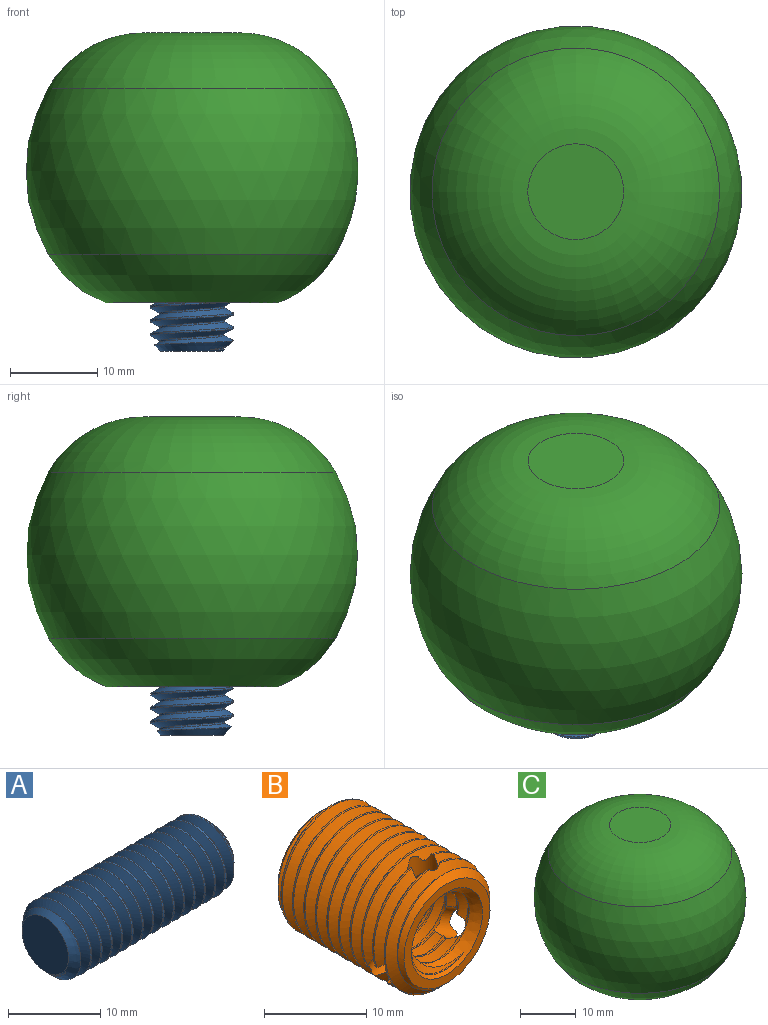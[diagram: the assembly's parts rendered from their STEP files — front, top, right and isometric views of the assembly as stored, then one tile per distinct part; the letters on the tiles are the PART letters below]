
ASSEMBLY  parts=3 mates=2
PART A: 9 faces, bbox 26.7x9.7x9.7 mm
  f0: cone r=4.76mm half-angle=45deg, axis (1,0,0), area 22.8mm2, adj f1,f4,f6,f7,f8
  f1: cone r=4.76mm half-angle=45deg, axis (1,0,0), area 1.2mm2, adj f0,f3,f6
  f2: cone r=3.57mm half-angle=45deg, axis (-1,0,0), area 24mm2, adj f3,f5,f6,f7,f8
  f3: cylinder r=4.76mm len=23.02mm, axis (1,0,0), area 85.9mm2, adj f1,f2,f6,f8
  f4: plane 7.14x7.14mm, normal (-1,0,0), area 40.1mm2, adj f0
  f5: plane 7.14x7.14mm, normal (1,0,0), area 40.1mm2, adj f2
  f6: bspline ~26.05x9.7mm, area 481.6mm2, adj f0,f1,f2,f3,f7
  f7: cylinder r=3.73mm len=25.08mm, axis (1,0,0), area 72.8mm2, adj f0,f2,f6,f8
  f8: bspline ~26.05x9.7mm, area 479.2mm2, adj f0,f2,f3,f7
PART B: 59 faces, bbox 14.5x18.5x14.5 mm
  f0: cylinder r=7.15mm len=9.12mm, axis (0,1,0), area 2.3mm2, adj f33,f44,f56,f57
  f1: cylinder r=7.15mm len=10.68mm, axis (0,1,0), area 2.4mm2, adj f34,f45,f57,f58
  f2: cylinder r=7.15mm len=9.5mm, axis (0,1,0), area 2.5mm2, adj f35,f46,f56,f58
  f3: cylinder r=7.15mm len=11.26mm, axis (0,1,0), area 2.5mm2, adj f31,f42,f57,f58
  f4: cylinder r=7.15mm len=14.3mm, axis (0,1,0), area 66mm2, adj f30,f42,f50,f57
  f5: cylinder r=7.15mm len=9.35mm, axis (0,1,0), area 2.4mm2, adj f32,f43,f56,f58
  f6: cylinder r=3.73mm len=3.72mm, axis (0,1,0), area 0.9mm2, adj f14,f27,f56,f57
  f7: cylinder r=3.73mm len=4.5mm, axis (0,1,0), area 0.9mm2, adj f15,f28,f57,f58
  f8: cylinder r=3.73mm len=4.3mm, axis (0,1,0), area 1.1mm2, adj f16,f29,f56,f58
  f9: cylinder r=3.73mm len=5.21mm, axis (0,1,0), area 1.1mm2, adj f12,f25,f57,f58
  f10: cylinder r=3.73mm len=11.78mm, axis (0,1,0), area 33.9mm2, adj f12,f24,f52,f57
  f11: cylinder r=3.73mm len=3.97mm, axis (0,1,0), area 0.9mm2, adj f13,f26,f56,f58
  f12: bspline ~13.25x9.18mm, area 210mm2, adj f9,f10,f18,f52,f57,f58
  f13: bspline ~6.86x4.21mm, area 6.1mm2, adj f11,f18,f56,f58
  f14: bspline ~6.08x4.06mm, area 5.5mm2, adj f6,f19,f56,f57
  f15: bspline ~6.49x2.01mm, area 5.5mm2, adj f7,f20,f57,f58
  f16: bspline ~6.03x4.05mm, area 5.9mm2, adj f8,f21,f56,f58
  f17: bspline ~9.18x9.18mm, area 22.1mm2, adj f22,f23,f49,f53,f56,f57
  f18: cylinder r=4.59mm len=12.99mm, axis (0,-1,0), area 80mm2, adj f12,f13,f24,f52,f56,f58
  f19: cylinder r=4.59mm len=5.5mm, axis (0,-1,0), area 2.8mm2, adj f14,f24,f56,f57
  f20: cylinder r=4.59mm len=6.02mm, axis (0,-1,0), area 2.6mm2, adj f15,f25,f57,f58
  f21: cylinder r=4.59mm len=5.16mm, axis (0,-1,0), area 2.6mm2, adj f16,f26,f56,f58
  f22: cylinder r=4.59mm len=5.69mm, axis (0,-1,0), area 2.7mm2, adj f17,f27,f56,f57
  f23: cylinder r=4.59mm len=9.18mm, axis (0,-1,0), area 12.6mm2, adj f17,f28,f29,f53,f57,f58
  f24: bspline ~13.65x9.18mm, area 207.3mm2, adj f10,f18,f19,f52,f56,f57
  f25: bspline ~6.11x1.88mm, area 5.9mm2, adj f9,f20,f57,f58
  f26: bspline ~5.1x3.31mm, area 5.5mm2, adj f11,f21,f56,f58
  f27: bspline ~6.18x3.92mm, area 5.5mm2, adj f6,f22,f56,f57
  f28: bspline ~7.17x2.7mm, area 6mm2, adj f7,f23,f57,f58
  f29: bspline ~9.18x9.18mm, area 20.2mm2, adj f8,f23,f49,f53,f56,f58
  f30: bspline ~14.47x14.47mm, area 392.9mm2, adj f4,f36,f37,f50,f56,f57
  f31: bspline ~12.66x4.41mm, area 13.2mm2, adj f3,f38,f57,f58
  f32: bspline ~10.71x6.97mm, area 12.8mm2, adj f5,f39,f56,f58
  f33: bspline ~10.61x6.95mm, area 13mm2, adj f0,f40,f56,f57
  f34: bspline ~11.1x3.53mm, area 13.7mm2, adj f1,f41,f57,f58
  f35: bspline ~14.47x14.47mm, area 40.3mm2, adj f2,f41,f48,f51,f56,f58
  f36: cylinder r=6.12mm len=13.09mm, axis (0,-1,0), area 44.7mm2, adj f30,f42,f43,f50,f56,f58
  f37: cylinder r=6.12mm len=7.76mm, axis (0,-1,0), area 2mm2, adj f30,f44,f56,f57
  f38: cylinder r=6.12mm len=8.74mm, axis (0,-1,0), area 1.9mm2, adj f31,f45,f57,f58
  f39: cylinder r=6.12mm len=7.52mm, axis (0,-1,0), area 1.9mm2, adj f32,f46,f56,f58
  f40: cylinder r=6.12mm len=7.95mm, axis (0,-1,0), area 2mm2, adj f33,f47,f56,f57
  f41: cylinder r=6.12mm len=12.24mm, axis (0,-1,0), area 9.3mm2, adj f34,f35,f47,f51,f57,f58
  f42: bspline ~14.47x14.47mm, area 386.8mm2, adj f3,f4,f36,f50,f57,f58
  f43: bspline ~10x5.94mm, area 13.8mm2, adj f5,f36,f56,f58
  f44: bspline ~9.1x5.86mm, area 13mm2, adj f0,f37,f56,f57
  f45: bspline ~12.27x4.03mm, area 12.8mm2, adj f1,f38,f57,f58
  f46: bspline ~9.35x6.23mm, area 13.2mm2, adj f2,f39,f56,f58
  f47: bspline ~14.29x14.28mm, area 46.4mm2, adj f40,f41,f48,f51,f56,f57
  f48: cylinder r=7.15mm len=14.26mm, axis (0,1,0), area 3.7mm2, adj f35,f47,f51,f56
  f49: cylinder r=3.73mm len=7.4mm, axis (0,1,0), area 1.8mm2, adj f17,f29,f53,f56
  f50: cone r=5.96mm half-angle=45deg, axis (0,-1,0), area 38.4mm2, adj f4,f30,f36,f42,f55
  f51: cone r=7.15mm half-angle=45deg, axis (0,1,0), area 38.4mm2, adj f35,f41,f47,f48,f54
  f52: cone r=3.73mm half-angle=45deg, axis (0,1,0), area 28.3mm2, adj f10,f12,f18,f24,f55
  f53: cone r=4.92mm half-angle=45deg, axis (0,-1,0), area 28.3mm2, adj f17,f23,f29,f49,f54
  f54: plane 11.92x11.92mm, normal (0,-1,0), area 35.5mm2, adj f51,f53
  f55: plane 11.92x11.92mm, normal (0,1,0), area 35.5mm2, adj f50,f52
  f56: cylinder r=1.59mm len=3.74mm, axis (0,0,-1), area 25.5mm2, adj f0,f2,f5,f6,f8,f11,f13,f14
  f57: cylinder r=1.59mm len=4.83mm, axis (0.87,0,0.5), area 25.8mm2, adj f0,f1,f3,f4,f6,f7,f9,f10
  f58: cylinder r=1.59mm len=4.72mm, axis (-0.87,0,0.5), area 22.6mm2, adj f1,f2,f3,f5,f7,f8,f9,f11
PART C: 9 faces, bbox 38.1x38.1x31 mm
  f0: plane 11x11mm, normal (0,0,1), area 95mm2, adj f2
  f1: sphere r=19.05mm, area 2280.2mm2, adj f2,f3
  f2: torus R=5.5mm, axis (0,0,1), area 966.2mm2, adj f0,f1
  f3: torus R=5.5mm, axis (0,0,1), area 750.4mm2, adj f1,f6
  f4: cylinder r=9.53mm len=19.05mm, axis (0,0,-1), area 129.4mm2, adj f5,f6
  f5: plane 19.05x19.05mm, normal (0,0,-1), area 142mm2, adj f4,f7
  f6: torus R=9.78mm, axis (0,0,1), area 29.6mm2, adj f3,f4
  f7: cylinder r=6.75mm len=17.46mm, axis (0,0,-1), area 740.3mm2, adj f5,f8
  f8: plane 13.49x13.49mm, normal (0,0,-1), area 143mm2, adj f7
PLACE A rot(axis=(0,-1,0),90deg) t=(0,0,11.11)mm
PLACE B rot(axis=(1,0,0),90deg) t=(0,0,23.81)mm
PLACE C at identity
MATE fastened B.f0 <-> C.f7  axis (0,0,1) through (0,0,23.81)mm
MATE fastened A.f0 <-> C.f7  axis (0,0,1) through (0,0,23.81)mm
